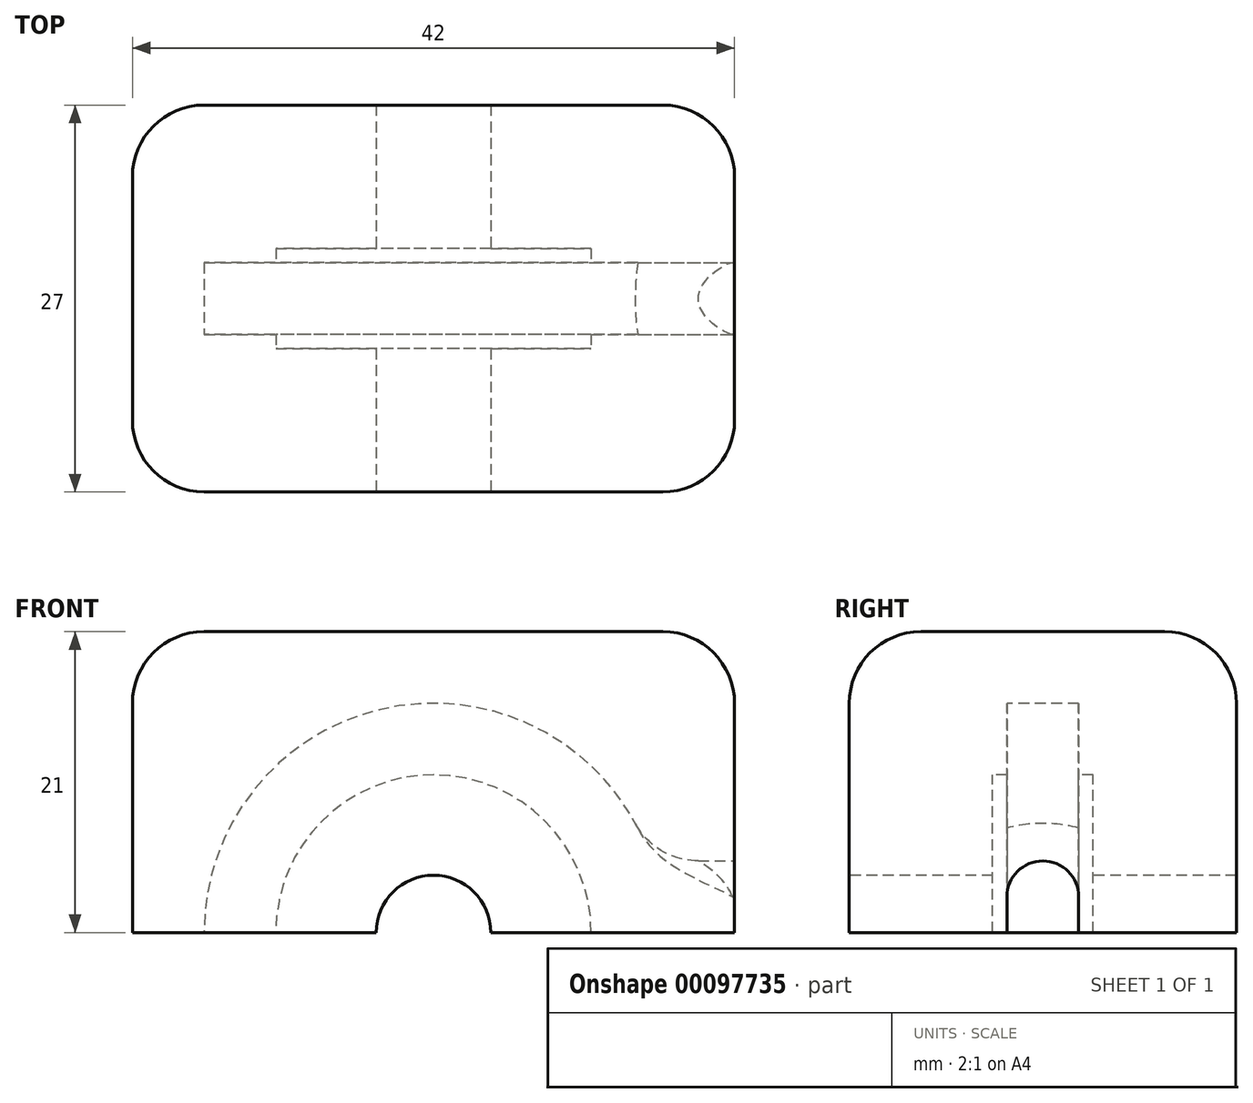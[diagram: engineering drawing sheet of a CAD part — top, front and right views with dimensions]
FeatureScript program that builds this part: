
annotation { "Feature Type Name" : "Feature", "Feature Type Description" : "" }
export const myFeature = defineFeature(function(context is Context, id is Id, definition is map)
    precondition{}
    {
        {
            assignVariable(context, id + "F0", {"name" : "dext_rlt", "anyValue" : 22});
        }
        {
            assignVariable(context, id + "F1", {"name" : "ep_rlt", "anyValue" : 7});
        }
        {
            assignVariable(context, id + "F2", {"name" : "d_cable", "anyValue" : 5});
        }
        {
            var Q0;
            Q0=qCreatedBy(makeId("Front.planeOp"),FACE);
            var sketch = newSketch(context, id + "F3", { "sketchPlane" : qUnion([Q0])});
            skLineSegment(sketch, "E0.bottom", {"start": v(-21, 0) * mm, "end": v(21, 0) * mm});
            skLineSegment(sketch, "E0.top", {"start": v(-21, 21) * mm, "end": v(21, 21) * mm});
            skLineSegment(sketch, "E0.left", {"start": v(-21, 0) * mm, "end": v(-21, 21) * mm});
            skLineSegment(sketch, "E0.right", {"start": v(21, 0) * mm, "end": v(21, 21) * mm});
            skSolve(sketch);
        }
        {
            var Q0;
            Q0=makeQuery(id+"F3.imprint","IMPRINT",FACE,{"disambiguationData":[TD([[makeQuery(id+"F3.imprint","IMPRINT",EDGE,{"derivedFrom":sQuery(id+"F3.wireOp",EDGE,"E0.bottom")}),1.0]])]});
            extrude(context, id + "F4", {"entities" : qUnion([Q0]), "endBound" : BoundingType.SYMMETRIC, "depth" : (getVariable(context, 'ep_rlt') + 20) * mm});
        }
        {
            var Q0;
            Q0=makeQuery(id+"F4.opExtrude","SWEPT_FACE",FACE,{"disambiguationData":[OSD([sQuery(id+"F3.wireOp",EDGE,"E0.right")])]});
            var sketch = newSketch(context, id + "F5", { "sketchPlane" : qUnion([Q0])});
            skArc(sketch, "E1", {"start": v(2.5, 2.5) * mm, "mid": v(0, 5) * mm, "end": v(-2.5, 2.5) * mm});
            skLineSegment(sketch, "E2", {"start": v(-2.5, 2.5) * mm, "end": v(-2.5, 0) * mm});
            skLineSegment(sketch, "E3", {"start": v(-2.5, 0) * mm, "end": v(2.5, 0) * mm});
            skLineSegment(sketch, "E4", {"start": v(2.5, 0) * mm, "end": v(2.5, 2.5) * mm});
            skSolve(sketch);
        }
        {
            var Q0;
            {var subQ0=sQuery(id+"F5.wireOp",EDGE,"E1");var subQ1=makeQuery(id+"F4.opExtrude","SWEPT_EDGE",EDGE,{"disambiguationData":[OSD([sQuery(id+"F3.wireOp",EDGE,"E0.bottom"),sQuery(id+"F3.wireOp",EDGE,"E0.right")])]});var subQ2=makeQuery(id+"F5.imprint","INTERSECT",VERTEX,{"disambiguationData":[OD(0.0)],"derivedFrom":[subQ1,subQ0]});Q0=makeQuery(id+"F5.imprint","IMPRINT",FACE,{"disambiguationData":[TD([[makeQuery(id+"F5.imprint","IMPRINT",EDGE,{"disambiguationData":[TD([[subQ2,-1.0]])],"derivedFrom":subQ0}),1.0]])]});}
            extrude(context, id + "F6", {"entities" : qUnion([Q0]), "operationType" : NewBodyOperationType.REMOVE, "oppositeDirection" : true, "depth" : (getVariable(context, 'dext_rlt') + 10) / 2 * mm});
        }
        {
            var Q0;
            Q0=qCreatedBy(makeId("Front.planeOp"),FACE);
            var sketch = newSketch(context, id + "F7", { "sketchPlane" : qUnion([Q0])});
            skCircle(sketch, "E5", {"center": v(0, 0) * mm, "radius": 11 * mm});
            skCircle(sketch, "E6", {"center": v(0, 0) * mm, "radius": 16 * mm});
            skSolve(sketch);
        }
        {
            var Q0;
            Q0=makeQuery(id+"F7.imprint","IMPRINT",FACE,{"disambiguationData":[TD([[makeQuery(id+"F7.imprint","IMPRINT",EDGE,{"derivedFrom":sQuery(id+"F7.wireOp",EDGE,"E5")}),1.0]])]});
            extrude(context, id + "F8", {"entities" : qUnion([Q0]), "operationType" : NewBodyOperationType.REMOVE, "endBound" : BoundingType.SYMMETRIC, "oppositeDirection" : true, "depth" : (getVariable(context, 'ep_rlt')) * mm});
        }
        {
            var Q0;
            Q0=makeQuery(id+"F7.imprint","IMPRINT",FACE,{"disambiguationData":[TD([[makeQuery(id+"F7.imprint","IMPRINT",EDGE,{"derivedFrom":sQuery(id+"F7.wireOp",EDGE,"E5")}),-1.0]])]});
            extrude(context, id + "F9", {"entities" : qUnion([Q0]), "operationType" : NewBodyOperationType.REMOVE, "endBound" : BoundingType.SYMMETRIC, "oppositeDirection" : true, "depth" : (getVariable(context, 'd_cable')) * mm});
        }
        {
            var Q0;
            Q0=makeQuery(id+"F9.boolean.opBoolean","INTERSECT",EDGE,{"derivedFrom":[makeQuery(id+"F6.boolean.opBoolean","COPY",FACE,{"derivedFrom":makeQuery(id+"F6.opExtrude","SWEPT_FACE",FACE,{"disambiguationData":[OSD([sQuery(id+"F5.wireOp",EDGE,"E1")])]})}),makeQuery(id+"F9.opExtrude","SWEPT_FACE",FACE,{"disambiguationData":[OSD([sQuery(id+"F7.wireOp",EDGE,"E6")])]})]});
            fillet(context, id + "F10", {"entities" : qUnion([Q0]), "radius" : 5 * mm, "tangentPropagation" : true, "allowEdgeOverflow" : false});
        }
        {
            var Q0;
            Q0=makeQuery(id+"F4.opExtrude","CAP_FACE",FACE,{"disambiguationData":[OSD([sQuery(id+"F3.wireOp",EDGE,"E0.bottom"),sQuery(id+"F3.wireOp",EDGE,"E0.top"),sQuery(id+"F3.wireOp",EDGE,"E0.left"),sQuery(id+"F3.wireOp",EDGE,"E0.right")])],"isStart":false});
            var sketch = newSketch(context, id + "F11", { "sketchPlane" : qUnion([Q0])});
            skCircle(sketch, "E7", {"center": v(0, 0) * mm, "radius": 4 * mm});
            skSolve(sketch);
        }
        {
            var Q0;
            {var subQ0=sQuery(id+"F11.wireOp",EDGE,"E7");var subQ1=makeQuery(id+"F4.opExtrude","CAP_EDGE",EDGE,{"disambiguationData":[OSD([sQuery(id+"F3.wireOp",EDGE,"E0.bottom")])],"isStart":false});var subQ2=makeQuery(id+"F11.imprint","INTERSECT",VERTEX,{"disambiguationData":[OD(0.0)],"derivedFrom":[subQ1,subQ0]});Q0=makeQuery(id+"F11.imprint","IMPRINT",FACE,{"disambiguationData":[TD([[makeQuery(id+"F11.imprint","IMPRINT",EDGE,{"disambiguationData":[TD([[subQ2,1.0]])],"derivedFrom":subQ0}),1.0]])]});}
            extrude(context, id + "F12", {"entities" : qUnion([Q0]), "operationType" : NewBodyOperationType.REMOVE, "endBound" : BoundingType.THROUGH_ALL, "oppositeDirection" : true, "depth" : 25 * mm});
        }
        {
            var Q0;
            Q0=makeQuery(id+"F4.opExtrude","SWEPT_FACE",FACE,{"disambiguationData":[OSD([sQuery(id+"F3.wireOp",EDGE,"E0.top")])]});
            var Q1;
            Q1=makeQuery(id+"F4.opExtrude","CAP_EDGE",EDGE,{"disambiguationData":[OSD([sQuery(id+"F3.wireOp",EDGE,"E0.right")])],"isStart":false});
            var Q2;
            Q2=makeQuery(id+"F4.opExtrude","CAP_EDGE",EDGE,{"disambiguationData":[OSD([sQuery(id+"F3.wireOp",EDGE,"E0.right")])],"isStart":true});
            var Q3;
            Q3=makeQuery(id+"F4.opExtrude","CAP_EDGE",EDGE,{"disambiguationData":[OSD([sQuery(id+"F3.wireOp",EDGE,"E0.left")])],"isStart":false});
            var Q4;
            Q4=makeQuery(id+"F4.opExtrude","CAP_EDGE",EDGE,{"disambiguationData":[OSD([sQuery(id+"F3.wireOp",EDGE,"E0.left")])],"isStart":true});
            fillet(context, id + "F13", {"entities" : qUnion([Q0, Q1, Q2, Q3, Q4]), "radius" : 5 * mm, "tangentPropagation" : true, "allowEdgeOverflow" : false});
        }
    });
